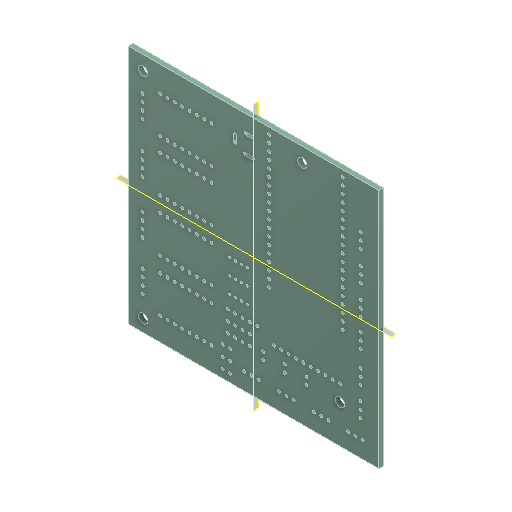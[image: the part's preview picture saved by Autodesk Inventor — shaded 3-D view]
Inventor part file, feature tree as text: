
AUTODESK INVENTOR PART (.ipt)
format: ipt  version: 2024.1 (Build 281209000, 209)  size: 373,760 bytes
history: native  units: mm
features: plane x2
ambient origin geometry x8: Origin, YZ Plane, XZ Plane, XY Plane, X Axis, Y Axis, Z Axis, Center Point
bodies: Volumenkörper1 (feature_tree)
feature tree (2):
  plane  "Arbeitsebene1"
  plane  "Arbeitsebene2"
